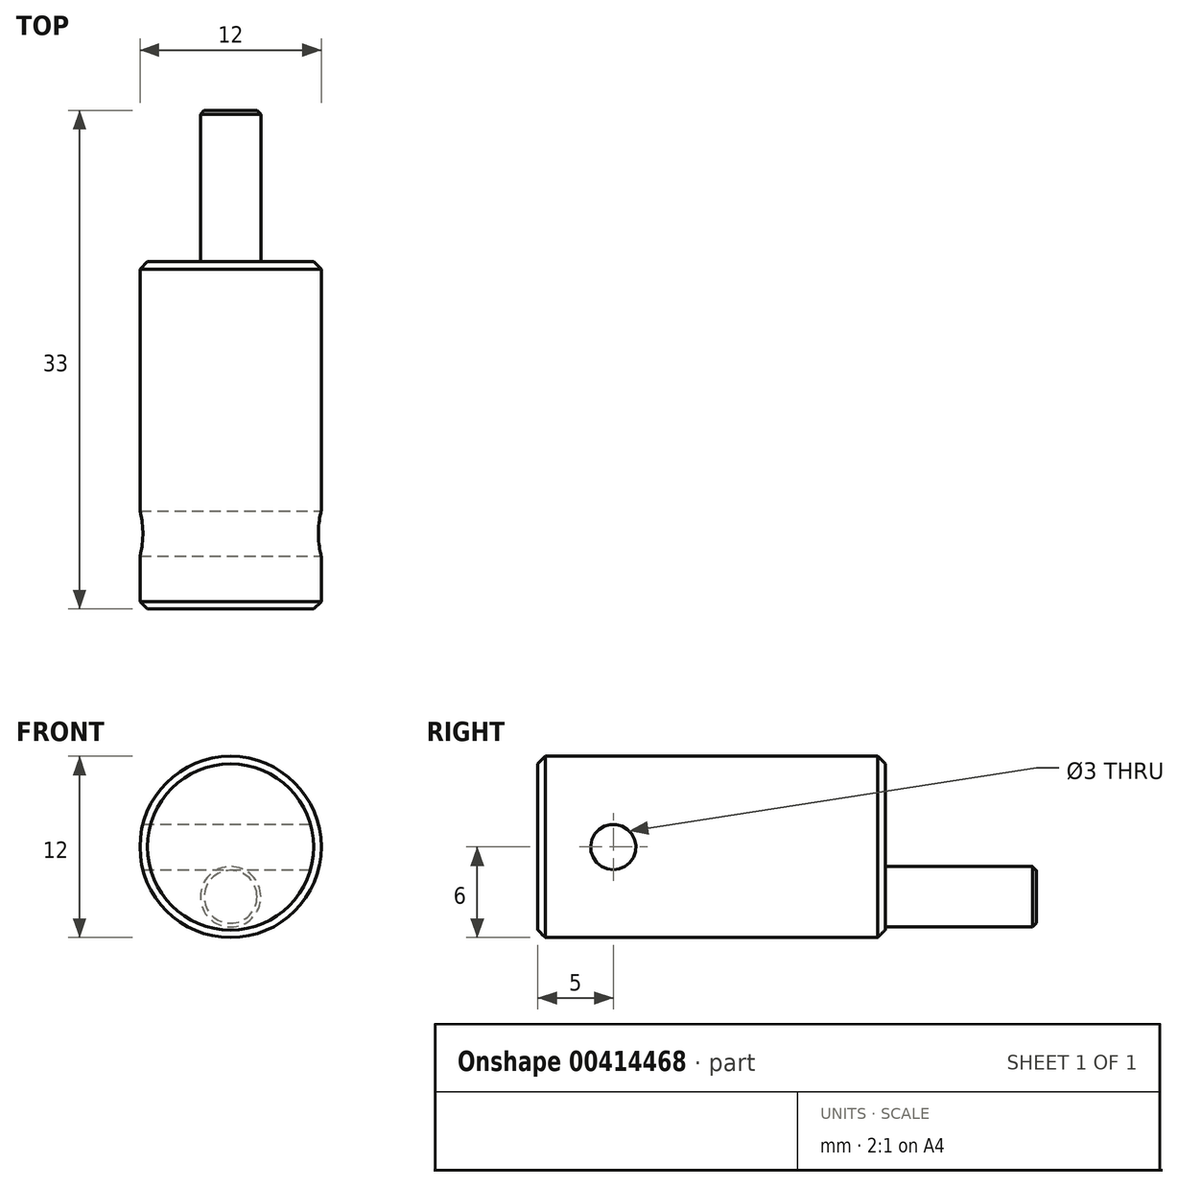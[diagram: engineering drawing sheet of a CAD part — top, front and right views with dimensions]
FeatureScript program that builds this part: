
annotation { "Feature Type Name" : "Feature", "Feature Type Description" : "" }
export const myFeature = defineFeature(function(context is Context, id is Id, definition is map)
    precondition{}
    {
        {
            var Q0;
            Q0=qCreatedBy(makeId("Front.planeOp"),FACE);
            var sketch = newSketch(context, id + "F0", { "sketchPlane" : qUnion([Q0])});
            skCircle(sketch, "E0", {"center": v(0, 0) * mm, "radius": 6 * mm});
            skSolve(sketch);
        }
        {
            var Q0;
            Q0=makeQuery(id+"F0.imprint","IMPRINT",FACE,{"disambiguationData":[TD([[makeQuery(id+"F0.imprint","IMPRINT",EDGE,{"derivedFrom":sQuery(id+"F0.wireOp",EDGE,"E0")}),1.0]])]});
            extrude(context, id + "F1", {"entities" : qUnion([Q0]), "depth" : 23 * mm});
        }
        {
            var Q0;
            Q0=makeQuery(id+"F1.opExtrude","CAP_EDGE",EDGE,{"disambiguationData":[OSD([sQuery(id+"F0.wireOp",EDGE,"E0")])],"isStart":false});
            var Q1;
            Q1=makeQuery(id+"F1.opExtrude","CAP_EDGE",EDGE,{"disambiguationData":[OSD([sQuery(id+"F0.wireOp",EDGE,"E0")])],"isStart":true});
            chamfer(context, id + "F2", {"entities" : qUnion([Q0, Q1]), "width" : .5 * mm, "tangentPropagation" : true});
        }
        {
            var Q0;
            Q0=qCreatedBy(makeId("Right.planeOp"),FACE);
            var sketch = newSketch(context, id + "F3", { "sketchPlane" : qUnion([Q0])});
            skCircle(sketch, "E1", {"center": v(-18, 0) * mm, "radius": 1.5 * mm});
            skSolve(sketch);
        }
        {
            var Q0;
            Q0=makeQuery(id+"F3.imprint","IMPRINT",FACE,{"disambiguationData":[TD([[makeQuery(id+"F3.imprint","IMPRINT",EDGE,{"derivedFrom":sQuery(id+"F3.wireOp",EDGE,"E1")}),1.0]])]});
            extrude(context, id + "F4", {"entities" : qUnion([Q0]), "operationType" : NewBodyOperationType.REMOVE, "endBound" : BoundingType.SYMMETRIC, "oppositeDirection" : true, "depth" : 25 * mm});
        }
        {
            var Q0;
            Q0=makeQuery(id+"F1.opExtrude","CAP_FACE",FACE,{"disambiguationData":[OSD([sQuery(id+"F0.wireOp",EDGE,"E0")])],"isStart":true});
            var sketch = newSketch(context, id + "F5", { "sketchPlane" : qUnion([Q0])});
            skCircle(sketch, "E2", {"center": v(0, -3.3) * mm, "radius": 2 * mm});
            skSolve(sketch);
        }
        {
            var Q0;
            Q0=makeQuery(id+"F5.imprint","IMPRINT",FACE,{"disambiguationData":[TD([[makeQuery(id+"F5.imprint","IMPRINT",EDGE,{"derivedFrom":sQuery(id+"F5.wireOp",EDGE,"E2")}),1.0]])]});
            extrude(context, id + "F6", {"entities" : qUnion([Q0]), "operationType" : NewBodyOperationType.ADD, "depth" : 10 * mm});
        }
        {
            var Q0;
            Q0=makeQuery(id+"F6.opExtrude","CAP_EDGE",EDGE,{"disambiguationData":[OSD([sQuery(id+"F5.wireOp",EDGE,"E2")])],"isStart":false});
            chamfer(context, id + "F7", {"entities" : qUnion([Q0]), "width" : .25 * mm, "tangentPropagation" : true});
        }
    });
